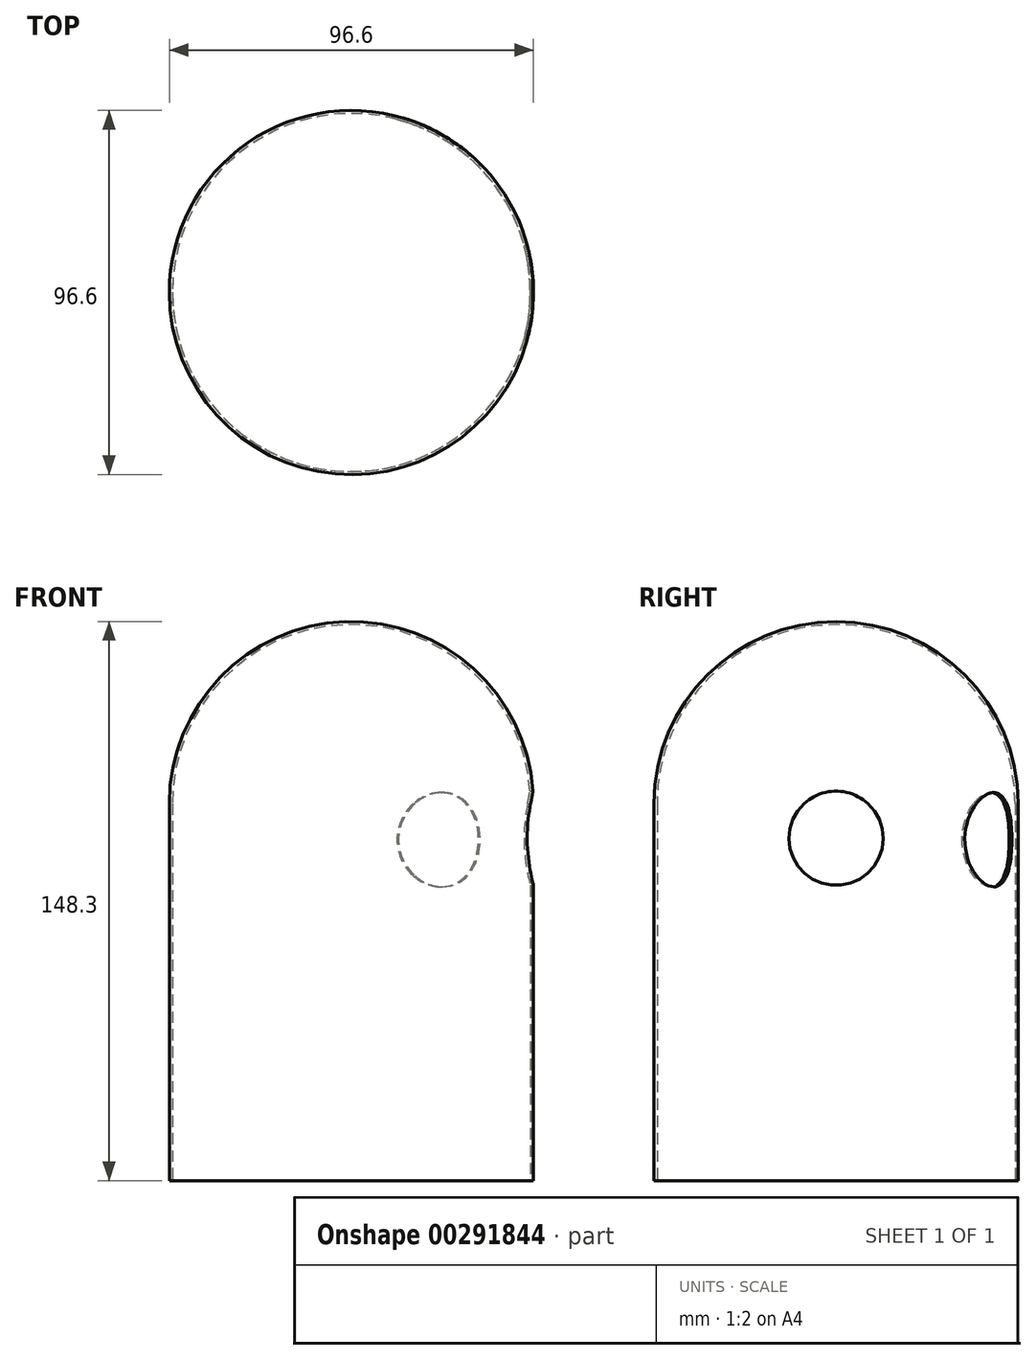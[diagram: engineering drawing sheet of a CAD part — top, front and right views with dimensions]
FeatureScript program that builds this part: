
annotation { "Feature Type Name" : "Feature", "Feature Type Description" : "" }
export const myFeature = defineFeature(function(context is Context, id is Id, definition is map)
    precondition{}
    {
        {
            var Q0;
            Q0=qCreatedBy(makeId("Top.planeOp"),FACE);
            var sketch = newSketch(context, id + "F0", { "sketchPlane" : qUnion([Q0])});
            skCircle(sketch, "E0", {"center": v(0, 0) * mm, "radius": 47.5 * mm});
            skCircle(sketch, "E1", {"center": v(0, 0) * mm, "radius": 48.3 * mm});
            skSolve(sketch);
        }
        {
            var Q0;
            Q0=makeQuery(id+"F0.imprint","IMPRINT",FACE,{"disambiguationData":[TD([[makeQuery(id+"F0.imprint","IMPRINT",EDGE,{"derivedFrom":sQuery(id+"F0.wireOp",EDGE,"E0")}),-1.0]])]});
            extrude(context, id + "F1", {"entities" : qUnion([Q0]), "depth" : 100 * mm});
        }
        {
            var Q0;
            Q0=makeQuery(id+"F1.opExtrude","CAP_FACE",FACE,{"disambiguationData":[OSD([sQuery(id+"F0.wireOp",EDGE,"E0"),sQuery(id+"F0.wireOp",EDGE,"E1")])],"isStart":false});
            var sketch = newSketch(context, id + "F2", { "sketchPlane" : qUnion([Q0])});
            skArc(sketch, "E2", {"start": v(-47.5, 0) * mm, "mid": v(0, -47.5) * mm, "end": v(47.5, 0) * mm});
            skArc(sketch, "E3", {"start": v(-48.3, 0) * mm, "mid": v(0, -48.3) * mm, "end": v(48.3, 0) * mm});
            skLineSegment(sketch, "E4", {"start": v(-48.3, 0) * mm, "end": v(-47.5, 0) * mm});
            skLineSegment(sketch, "E5", {"start": v(47.5, 0) * mm, "end": v(48.3, 0) * mm});
            skLineSegment(sketch, "E6", {"start": v(-47.5, 0) * mm, "end": v(47.5, 0) * mm, "construction": true});
            skSolve(sketch);
        }
        {
            var Q0;
            Q0=makeQuery(id+"F2.imprint","IMPRINT",FACE,{"disambiguationData":[TD([[makeQuery(id+"F2.imprint","IMPRINT",EDGE,{"derivedFrom":sQuery(id+"F2.wireOp",EDGE,"E2")}),-1.0]])]});
            var Q1;
            Q1=sQuery(id+"F2.wireOp",EDGE,"E4");
            revolve(context, id + "F3", {"operationType" : NewBodyOperationType.ADD, "entities" : qUnion([Q0]), "axis" : qUnion([Q1]), "revolveType" : RevolveType.ONE_DIRECTION, "oppositeDirection" : true, "angle" : 180 * degree});
        }
        {
            var Q0;
            Q0=qCreatedBy(makeId("Right.planeOp"),FACE);
            cPlane(context, id + "F4", {"entities" : qUnion([Q0]), "cplaneType" : CPlaneType.OFFSET, "offset" : 49 * mm, "width" : 150 * mm, "height" : 150 * mm});
        }
        {
            var Q0;
            Q0=qCreatedBy(id+"F4.planeOp",FACE);
            var sketch = newSketch(context, id + "F5", { "sketchPlane" : qUnion([Q0])});
            skCircle(sketch, "E7", {"center": v(0, 90.81) * mm, "radius": 12.5 * mm});
            skSolve(sketch);
        }
        {
            var Q0;
            Q0=makeQuery(id+"F5.imprint","IMPRINT",FACE,{"disambiguationData":[TD([[makeQuery(id+"F5.imprint","IMPRINT",EDGE,{"derivedFrom":sQuery(id+"F5.wireOp",EDGE,"E7")}),1.0]])]});
            extrude(context, id + "F6", {"entities" : qUnion([Q0]), "operationType" : NewBodyOperationType.REMOVE, "oppositeDirection" : true, "depth" : 6 * mm});
        }
        {
            var Q0;
            Q0=makeQuery(id+"F1.opExtrude","SWEPT_FACE",FACE,{"disambiguationData":[OSD([sQuery(id+"F0.wireOp",EDGE,"E1")])]});
            cPlane(context, id + "F7", {"entities" : qUnion([Q0]), "cplaneType" : CPlaneType.LINE_ANGLE, "offset" : 25 * mm, "angle" : 120 * degree, "width" : 150 * mm, "height" : 150 * mm});
        }
        {
            var Q0;
            Q0=qCreatedBy(id+"F7.planeOp",FACE);
            cPlane(context, id + "F8", {"entities" : qUnion([Q0]), "cplaneType" : CPlaneType.OFFSET, "offset" : 49 * mm, "width" : 150 * mm, "height" : 150 * mm});
        }
        {
            var Q0;
            Q0=qCreatedBy(id+"F8.planeOp",FACE);
            var sketch = newSketch(context, id + "F9", { "sketchPlane" : qUnion([Q0])});
            skCircle(sketch, "E8", {"center": v(0, 90.43) * mm, "radius": 12.5 * mm});
            skSolve(sketch);
        }
        {
            var Q0;
            Q0=makeQuery(id+"F9.imprint","IMPRINT",FACE,{"disambiguationData":[TD([[makeQuery(id+"F9.imprint","IMPRINT",EDGE,{"derivedFrom":sQuery(id+"F9.wireOp",EDGE,"E8")}),1.0]])]});
            extrude(context, id + "F10", {"entities" : qUnion([Q0]), "operationType" : NewBodyOperationType.REMOVE, "oppositeDirection" : true, "depth" : 6 * mm});
        }
    });
